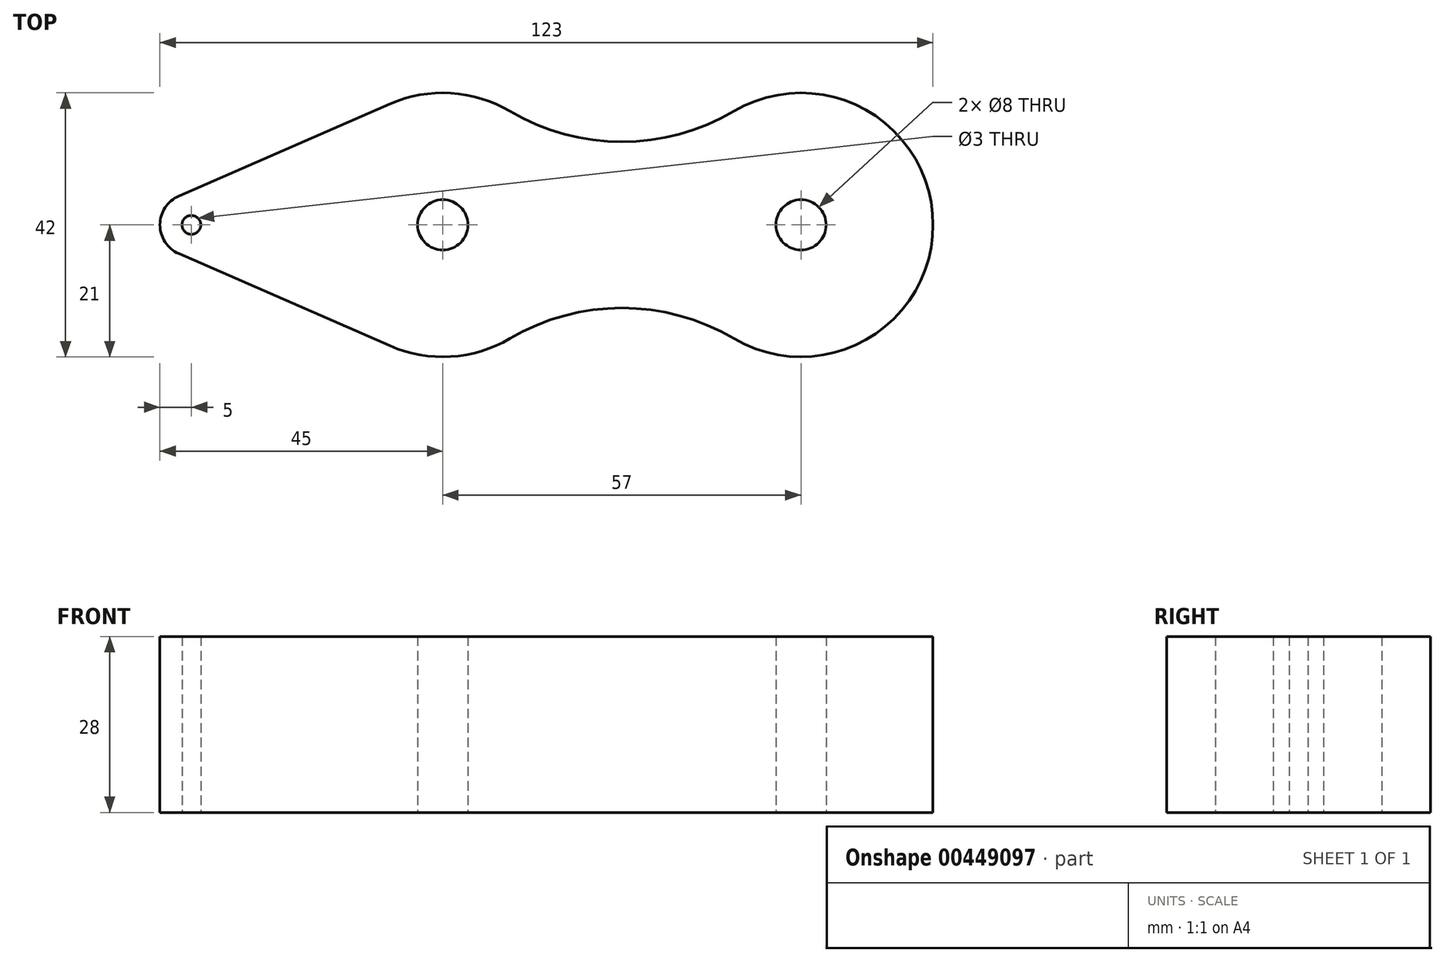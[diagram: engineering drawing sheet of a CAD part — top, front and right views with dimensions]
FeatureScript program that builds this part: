
annotation { "Feature Type Name" : "Feature", "Feature Type Description" : "" }
export const myFeature = defineFeature(function(context is Context, id is Id, definition is map)
    precondition{}
    {
        {
            var Q0;
            Q0=qCreatedBy(makeId("Top.planeOp"),FACE);
            var sketch = newSketch(context, id + "F0", { "sketchPlane" : qUnion([Q0])});
            skArc(sketch, "E0", {"start": v(-122.4, -19.25) * mm, "mid": v(-112.73, -20.96) * mm, "end": v(-103.34, -18.1) * mm});
            skArc(sketch, "E1", {"start": v(-156, 4.58) * mm, "mid": v(-159, 0) * mm, "end": v(-156, -4.58) * mm});
            skLineSegment(sketch, "E2", {"start": v(-156, -4.58) * mm, "end": v(-122.4, -19.25) * mm});
            skLineSegment(sketch, "E3", {"start": v(-156, 4.58) * mm, "end": v(-122.4, 19.25) * mm});
            skCircle(sketch, "E4", {"center": v(-114, 0) * mm, "radius": 4 * mm});
            skCircle(sketch, "E5", {"center": v(-57, 0) * mm, "radius": 4 * mm});
            skArc(sketch, "E6.trimOffspring", {"start": v(-103.34, 18.1) * mm, "mid": v(-112.73, 20.96) * mm, "end": v(-122.4, 19.25) * mm});
            skArc(sketch, "E7.1.0.0", {"start": v(-103.34, 18.1) * mm, "mid": v(-85.5, 13.22) * mm, "end": v(-67.66, 18.1) * mm});
            skArc(sketch, "E8.MirrorCS", {"start": v(-103.34, -18.1) * mm, "mid": v(-85.5, -13.22) * mm, "end": v(-67.66, -18.1) * mm});
            skCircle(sketch, "E9", {"center": v(-154, 0) * mm, "radius": 1.5 * mm});
            skArc(sketch, "E10", {"start": v(-67.66, -18.1) * mm, "mid": v(-36, 0) * mm, "end": v(-67.66, 18.1) * mm});
            skSolve(sketch);
        }
        {
            var Q0;
            Q0=makeQuery(id+"F0.imprint","IMPRINT",FACE,{"disambiguationData":[TD([[makeQuery(id+"F0.imprint","IMPRINT",EDGE,{"derivedFrom":sQuery(id+"F0.wireOp",EDGE,"E0")}),1.0]])]});
            extrude(context, id + "F1", {"entities" : qUnion([Q0]), "depth" : 28 * mm});
        }
    });
